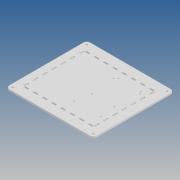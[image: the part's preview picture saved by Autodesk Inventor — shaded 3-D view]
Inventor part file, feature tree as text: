
AUTODESK INVENTOR PART (.ipt)
format: ipt  version: 2020 (Build 240168000, 168)  size: 269,824 bytes
history: native  units: mm
features: reference x8, other x7, extrude x7, sketch x7, pattern_linear x4
ambient origin geometry x8: Origin, YZ Plane, XZ Plane, XY Plane, X Axis, Y Axis, Z Axis, Center Point
bodies: Body1 (feature_tree)
feature tree (33):
  other  "Твердое тело1"
  extrude  "Выдавливание1"  Depth=175.0mm
  extrude  "Выдавливание3"  Depth=161.0mm
  pattern_linear  "Прямоуг.массив1"  Spacing1=4.0mm  [1 undecoded]
  extrude  "Выдавливание4"  Depth=4.0mm
  pattern_linear  "Прямоуг.массив2"  Spacing1=4.0mm  [1 undecoded]
  extrude  "Выдавливание5"  Depth=4.0mm
  pattern_linear  "Прямоуг.массив3"  Spacing1=15.0mm  [1 undecoded]
  extrude  "Выдавливание6"  Depth=15.0mm
  pattern_linear  "Прямоуг.массив4"  Spacing1=15.0mm  [1 undecoded]
  extrude  "Выдавливание7"  Depth=15.0mm
  extrude  "Выдавливание8"  Depth=3.0mm TaperAngle=0.0deg
  sketch  "Эскиз1"
  sketch  "Эскиз3"
  sketch  "Эскиз4"
  sketch  "Эскиз5"
  sketch  "Эскиз6"
  sketch  "Эскиз7"
  reference  "Ссылка1"
  reference  "Ссылка2"
  reference  "Ссылка3"
  reference  "Ссылка4"
  sketch  "Эскиз8"
  reference  "Ссылка5"
  reference  "Ссылка6"
  reference  "Ссылка7"
  reference  "Ссылка8"
  other  "<path> - Electronic box.iam"
  other  "000.100 - Electronic box.iam"
  other  "Raspberry-Pi-4-Model-B-03:1"
  other  "Jetson nano_fixed:1"
  other  "142-13449-1000-A02_ASM:1"
  other  "142-13449-1000-A02:1"
note: 4 required parameter values undecoded (feature->parameter linkage not recoverable at this tier; creation-order binding heuristic only, values carry confidence <= 0.55)
note: 1 file-system path scrubbed to <path> (originals preserved in map.json)
